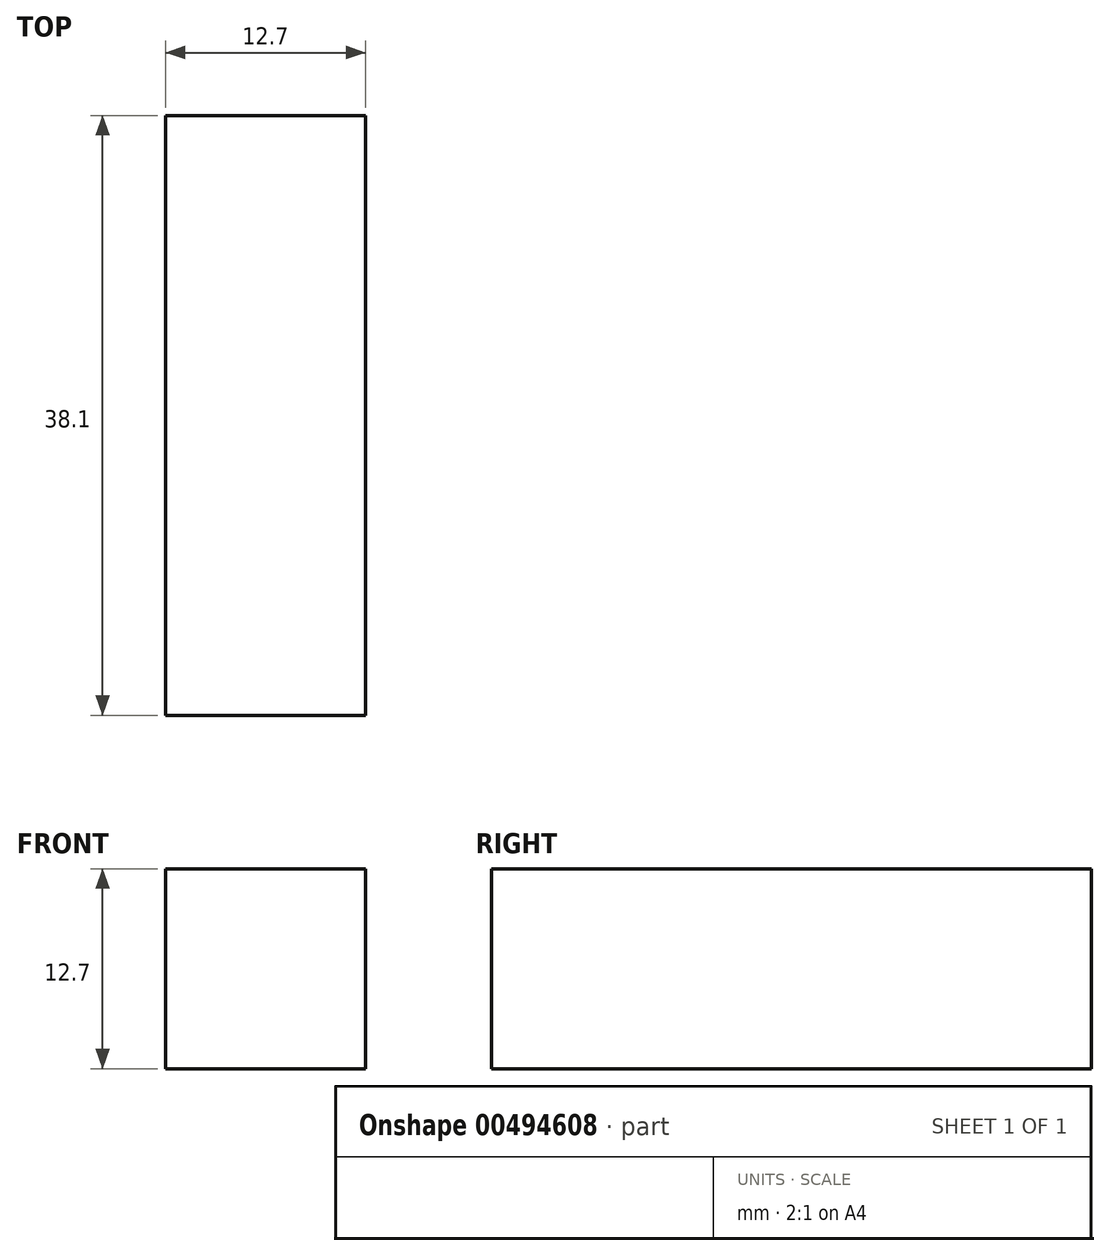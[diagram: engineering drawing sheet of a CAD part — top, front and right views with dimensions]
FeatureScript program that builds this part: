
annotation { "Feature Type Name" : "Feature", "Feature Type Description" : "" }
export const myFeature = defineFeature(function(context is Context, id is Id, definition is map)
    precondition{}
    {
        {
            var Q0;
            Q0=qCreatedBy(makeId("Front.planeOp"),FACE);
            var sketch = newSketch(context, id + "F0", { "sketchPlane" : qUnion([Q0])});
            skLineSegment(sketch, "E0.bottom", {"start": v(-6.35, 6.35) * mm, "end": v(6.35, 6.35) * mm});
            skLineSegment(sketch, "E0.top", {"start": v(-6.35, -6.35) * mm, "end": v(6.35, -6.35) * mm});
            skLineSegment(sketch, "E0.left", {"start": v(-6.35, 6.35) * mm, "end": v(-6.35, -6.35) * mm});
            skLineSegment(sketch, "E0.right", {"start": v(6.35, 6.35) * mm, "end": v(6.35, -6.35) * mm});
            skLineSegment(sketch, "E1", {"start": v(-6.35, 6.35) * mm, "end": v(6.35, -6.35) * mm, "construction": true});
            skPoint(sketch, "E2", {"position": v(0, 0) * mm});
            skSolve(sketch);
        }
        {
            var Q0;
            Q0=makeQuery(id+"F0.imprint","IMPRINT",FACE,{"disambiguationData":[TD([[makeQuery(id+"F0.imprint","IMPRINT",EDGE,{"derivedFrom":sQuery(id+"F0.wireOp",EDGE,"E0.bottom")}),-1.0]])]});
            extrude(context, id + "F1", {"entities" : qUnion([Q0]), "depth" : 38.1 * mm, "offsetDistance" : 25.4 * mm});
        }
    });
